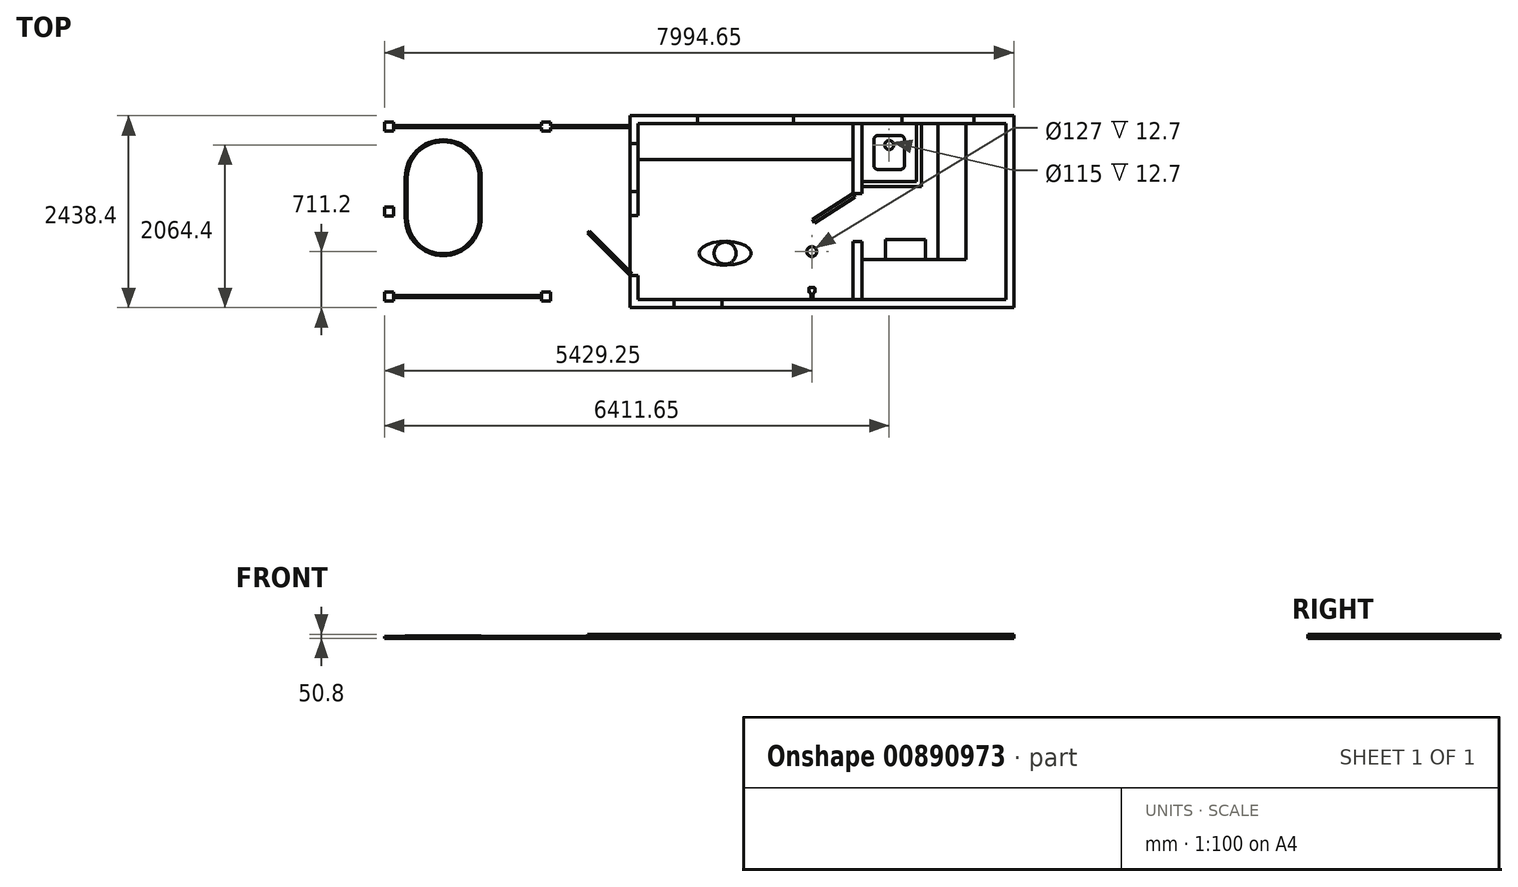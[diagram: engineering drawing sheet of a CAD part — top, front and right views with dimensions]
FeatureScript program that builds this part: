
annotation { "Feature Type Name" : "Feature", "Feature Type Description" : "" }
export const myFeature = defineFeature(function(context is Context, id is Id, definition is map)
    precondition{}
    {
        {
            var Q0;
            Q0=qCreatedBy(makeId("Top.planeOp"),FACE);
            var sketch = newSketch(context, id + "F0", { "sketchPlane" : qUnion([Q0])});
            skLineSegment(sketch, "E0.bottom", {"start": v(-2438.4, -1219.2) * mm, "end": v(2438.4, -1219.2) * mm});
            skLineSegment(sketch, "E0.top", {"start": v(-2438.4, 1219.2) * mm, "end": v(2438.4, 1219.2) * mm});
            skLineSegment(sketch, "E0.left", {"start": v(-2438.4, -1219.2) * mm, "end": v(-2438.4, 1219.2) * mm});
            skLineSegment(sketch, "E0.right", {"start": v(2438.4, -1219.2) * mm, "end": v(2438.4, 1219.2) * mm});
            skPoint(sketch, "E0.middle", {"position": v(0, 0) * mm});
            skSolve(sketch);
        }
        {
            var Q0;
            Q0=qSketchRegion(id+"F0",true);
            extrude(context, id + "F1", {"entities" : qUnion([Q0]), "depth" : 25.4 * mm, "offsetDistance" : 25.4 * mm});
        }
        {
            var Q0;
            Q0=makeQuery(id+"F1.opExtrude","CAP_FACE",FACE,{"disambiguationData":[OSD([sQuery(id+"F0.wireOp",EDGE,"E0.bottom"),sQuery(id+"F0.wireOp",EDGE,"E0.top"),sQuery(id+"F0.wireOp",EDGE,"E0.left"),sQuery(id+"F0.wireOp",EDGE,"E0.right")])],"isStart":false});
            var sketch = newSketch(context, id + "F2", { "sketchPlane" : qUnion([Q0])});
            skLineSegment(sketch, "E1.0", {"start": v(-2438.4, 1219.2) * mm, "end": v(2438.4, 1219.2) * mm});
            skLineSegment(sketch, "E2.0", {"start": v(-2438.4, -1219.2) * mm, "end": v(-2438.4, 1219.2) * mm});
            skLineSegment(sketch, "E3.0", {"start": v(-2438.4, -1219.2) * mm, "end": v(2438.4, -1219.2) * mm});
            skLineSegment(sketch, "E4.0", {"start": v(2438.4, -1219.2) * mm, "end": v(2438.4, 1219.2) * mm});
            skLineSegment(sketch, "E5.bottom", {"start": v(-2336.8, 1117.6) * mm, "end": v(2336.8, 1117.6) * mm});
            skLineSegment(sketch, "E5.top", {"start": v(-2336.8, -1117.6) * mm, "end": v(2336.8, -1117.6) * mm});
            skLineSegment(sketch, "E5.left", {"start": v(-2336.8, 1117.6) * mm, "end": v(-2336.8, -1117.6) * mm});
            skLineSegment(sketch, "E5.right", {"start": v(2336.8, 1117.6) * mm, "end": v(2336.8, -1117.6) * mm});
            skPoint(sketch, "E5.middle", {"position": v(0, 0) * mm});
            skSolve(sketch);
        }
        {
            var Q0;
            Q0=qSketchRegion(id+"F2",true);
            extrude(context, id + "F3", {"entities" : qUnion([Q0]), "depth" : 25.4 * mm, "offsetDistance" : 25.4 * mm});
        }
        {
            var Q0;
            Q0=makeQuery(id+"F1.opExtrude","CAP_FACE",FACE,{"disambiguationData":[OSD([sQuery(id+"F0.wireOp",EDGE,"E0.bottom"),sQuery(id+"F0.wireOp",EDGE,"E0.top"),sQuery(id+"F0.wireOp",EDGE,"E0.left"),sQuery(id+"F0.wireOp",EDGE,"E0.right")])],"isStart":false});
            var sketch = newSketch(context, id + "F4", { "sketchPlane" : qUnion([Q0])});
            skLineSegment(sketch, "E6.bottom", {"start": v(393.7, 1117.6) * mm, "end": v(508, 1117.6) * mm});
            skLineSegment(sketch, "E6.top", {"start": v(393.7, -1117.6) * mm, "end": v(508, -1117.6) * mm});
            skLineSegment(sketch, "E6.left", {"start": v(393.7, 1117.6) * mm, "end": v(393.7, -1117.6) * mm});
            skLineSegment(sketch, "E6.right", {"start": v(508, 1117.6) * mm, "end": v(508, -1117.6) * mm});
            skSolve(sketch);
        }
        {
            var Q0;
            Q0=qSketchRegion(id+"F4",true);
            extrude(context, id + "F5", {"entities" : qUnion([Q0]), "depth" : 25.4 * mm, "offsetDistance" : 25.4 * mm});
        }
        {
            var Q0;
            Q0=makeQuery(id+"F5.opExtrude","CAP_FACE",FACE,{"disambiguationData":[OSD([sQuery(id+"F4.wireOp",EDGE,"E6.bottom"),sQuery(id+"F4.wireOp",EDGE,"E6.top"),sQuery(id+"F4.wireOp",EDGE,"E6.left"),sQuery(id+"F4.wireOp",EDGE,"E6.right")])],"isStart":false});
            var sketch = newSketch(context, id + "F6", { "sketchPlane" : qUnion([Q0])});
            skLineSegment(sketch, "E7.bottom", {"start": v(393.7, 228.6) * mm, "end": v(508, 228.6) * mm});
            skLineSegment(sketch, "E7.top", {"start": v(393.7, -381) * mm, "end": v(508, -381) * mm});
            skLineSegment(sketch, "E7.left", {"start": v(393.7, 228.6) * mm, "end": v(393.7, -381) * mm});
            skLineSegment(sketch, "E7.right", {"start": v(508, 228.6) * mm, "end": v(508, -381) * mm});
            skSolve(sketch);
        }
        {
            var Q0;
            Q0=qSketchRegion(id+"F6",true);
            extrude(context, id + "F7", {"entities" : qUnion([Q0]), "operationType" : NewBodyOperationType.REMOVE, "oppositeDirection" : true, "depth" : 25.4 * mm, "offsetDistance" : 25.4 * mm});
        }
        {
            var Q0;
            Q0=makeQuery(id+"F3.opExtrude","CAP_FACE",FACE,{"disambiguationData":[OSD([sQuery(id+"F2.wireOp",EDGE,"E1.0"),sQuery(id+"F2.wireOp",EDGE,"E2.0"),sQuery(id+"F2.wireOp",EDGE,"E3.0"),sQuery(id+"F2.wireOp",EDGE,"E4.0"),sQuery(id+"F2.wireOp",EDGE,"E5.bottom"),sQuery(id+"F2.wireOp",EDGE,"E5.top"),sQuery(id+"F2.wireOp",EDGE,"E5.left"),sQuery(id+"F2.wireOp",EDGE,"E5.right")])],"isStart":false});
            var sketch = newSketch(context, id + "F8", { "sketchPlane" : qUnion([Q0])});
            skLineSegment(sketch, "E8.bottom", {"start": v(-2438.4, -812.8) * mm, "end": v(-2336.8, -812.8) * mm});
            skLineSegment(sketch, "E8.top", {"start": v(-2438.4, -50.8) * mm, "end": v(-2336.8, -50.8) * mm});
            skLineSegment(sketch, "E8.left", {"start": v(-2438.4, -812.8) * mm, "end": v(-2438.4, -50.8) * mm});
            skLineSegment(sketch, "E8.right", {"start": v(-2336.8, -812.8) * mm, "end": v(-2336.8, -50.8) * mm});
            skSolve(sketch);
        }
        {
            var Q0;
            Q0=qSketchRegion(id+"F8",true);
            extrude(context, id + "F9", {"entities" : qUnion([Q0]), "operationType" : NewBodyOperationType.REMOVE, "oppositeDirection" : true, "depth" : 25.4 * mm, "offsetDistance" : 25.4 * mm});
        }
        {
            var Q0;
            Q0=makeQuery(id+"F1.opExtrude","CAP_FACE",FACE,{"disambiguationData":[OSD([sQuery(id+"F0.wireOp",EDGE,"E0.bottom"),sQuery(id+"F0.wireOp",EDGE,"E0.top"),sQuery(id+"F0.wireOp",EDGE,"E0.left"),sQuery(id+"F0.wireOp",EDGE,"E0.right")])],"isStart":false});
            var sketch = newSketch(context, id + "F10", { "sketchPlane" : qUnion([Q0])});
            skLineSegment(sketch, "E9.bottom", {"start": v(711.2, 965.2) * mm, "end": v(999.6, 965.2) * mm});
            skLineSegment(sketch, "E9.top", {"start": v(711.2, 535.2) * mm, "end": v(999.6, 535.2) * mm});
            skLineSegment(sketch, "E9.left", {"start": v(660.4, 914.4) * mm, "end": v(660.4, 586) * mm});
            skLineSegment(sketch, "E9.right", {"start": v(1050.4, 914.4) * mm, "end": v(1050.4, 586) * mm});
            skPoint(sketch, "E10.visualSharp", {"position": v(660.4, 965.2) * mm});
            skArc(sketch, "E10.filletArc", {"start": v(711.2, 965.2) * mm, "mid": v(675.28, 950.32) * mm, "end": v(660.4, 914.4) * mm});
            skPoint(sketch, "E11.visualSharp", {"position": v(1050.4, 965.2) * mm});
            skArc(sketch, "E11.filletArc", {"start": v(1050.4, 914.4) * mm, "mid": v(1035.52, 950.32) * mm, "end": v(999.6, 965.2) * mm});
            skPoint(sketch, "E12.visualSharp", {"position": v(1050.4, 535.2) * mm});
            skArc(sketch, "E12.filletArc", {"start": v(999.6, 535.2) * mm, "mid": v(1035.52, 550.08) * mm, "end": v(1050.4, 586) * mm});
            skPoint(sketch, "E13.visualSharp", {"position": v(660.4, 535.2) * mm});
            skArc(sketch, "E13.filletArc", {"start": v(660.4, 586) * mm, "mid": v(675.28, 550.08) * mm, "end": v(711.2, 535.2) * mm});
            skSolve(sketch);
        }
        {
            var Q0;
            Q0=qSketchRegion(id+"F10",true);
            extrude(context, id + "F11", {"entities" : qUnion([Q0]), "depth" : 25.4 * mm, "offsetDistance" : 25.4 * mm});
        }
        {
            var Q0;
            Q0=makeQuery(id+"F1.opExtrude","CAP_FACE",FACE,{"disambiguationData":[OSD([sQuery(id+"F0.wireOp",EDGE,"E0.bottom"),sQuery(id+"F0.wireOp",EDGE,"E0.top"),sQuery(id+"F0.wireOp",EDGE,"E0.left"),sQuery(id+"F0.wireOp",EDGE,"E0.right")])],"isStart":false});
            var sketch = newSketch(context, id + "F12", { "sketchPlane" : qUnion([Q0])});
            skLineSegment(sketch, "E14", {"start": v(508, -1117.6) * mm, "end": v(2336.8, -1117.6) * mm});
            skLineSegment(sketch, "E15", {"start": v(2336.8, -1117.6) * mm, "end": v(2336.8, 1117.6) * mm});
            skLineSegment(sketch, "E16", {"start": v(2336.8, 1117.6) * mm, "end": v(1828.8, 1117.6) * mm});
            skLineSegment(sketch, "E17", {"start": v(1828.8, 1117.6) * mm, "end": v(1828.8, -609.6) * mm});
            skLineSegment(sketch, "E18", {"start": v(1828.8, -609.6) * mm, "end": v(508, -609.6) * mm});
            skLineSegment(sketch, "E19", {"start": v(508, -609.6) * mm, "end": v(508, -1117.6) * mm});
            skSolve(sketch);
        }
        {
            var Q0;
            Q0=qSketchRegion(id+"F12",true);
            extrude(context, id + "F13", {"entities" : qUnion([Q0]), "depth" : 25.4 * mm, "offsetDistance" : 25.4 * mm});
        }
        {
            var Q0;
            Q0=makeQuery(id+"F1.opExtrude","CAP_FACE",FACE,{"disambiguationData":[OSD([sQuery(id+"F0.wireOp",EDGE,"E0.bottom"),sQuery(id+"F0.wireOp",EDGE,"E0.top"),sQuery(id+"F0.wireOp",EDGE,"E0.left"),sQuery(id+"F0.wireOp",EDGE,"E0.right")])],"isStart":false});
            var sketch = newSketch(context, id + "F14", { "sketchPlane" : qUnion([Q0])});
            skLineSegment(sketch, "E20.0", {"start": v(1828.8, -609.6) * mm, "end": v(1473.2, -609.6) * mm});
            skLineSegment(sketch, "E21.0", {"start": v(1828.8, 1117.6) * mm, "end": v(1828.8, -609.6) * mm});
            skLineSegment(sketch, "E22", {"start": v(1473.2, -609.6) * mm, "end": v(1473.2, 1117.6) * mm});
            skLineSegment(sketch, "E23", {"start": v(1473.2, 1117.6) * mm, "end": v(1828.8, 1117.6) * mm});
            skSolve(sketch);
        }
        {
            var Q0;
            Q0=qSketchRegion(id+"F14",true);
            extrude(context, id + "F15", {"entities" : qUnion([Q0]), "depth" : 12.7 * mm, "offsetDistance" : 25.4 * mm});
        }
        {
            var Q0;
            Q0=makeQuery(id+"F1.opExtrude","CAP_FACE",FACE,{"disambiguationData":[OSD([sQuery(id+"F0.wireOp",EDGE,"E0.bottom"),sQuery(id+"F0.wireOp",EDGE,"E0.top"),sQuery(id+"F0.wireOp",EDGE,"E0.left"),sQuery(id+"F0.wireOp",EDGE,"E0.right")])],"isStart":false});
            var sketch = newSketch(context, id + "F16", { "sketchPlane" : qUnion([Q0])});
            skLineSegment(sketch, "E24.bottom", {"start": v(393.7, 228.6) * mm, "end": v(-117.99, -102.75) * mm});
            skLineSegment(sketch, "E24.top", {"start": v(421.31, 185.96) * mm, "end": v(-90.37, -145.39) * mm});
            skLineSegment(sketch, "E24.left", {"start": v(393.7, 228.6) * mm, "end": v(421.31, 185.96) * mm});
            skLineSegment(sketch, "E24.right", {"start": v(-117.99, -102.75) * mm, "end": v(-90.37, -145.39) * mm});
            skSolve(sketch);
        }
        {
            var Q0;
            Q0=qSketchRegion(id+"F16",true);
            extrude(context, id + "F17", {"entities" : qUnion([Q0]), "depth" : 25.4 * mm, "offsetDistance" : 25.4 * mm});
        }
        {
            var Q0;
            Q0=makeQuery(id+"F1.opExtrude","CAP_FACE",FACE,{"disambiguationData":[OSD([sQuery(id+"F0.wireOp",EDGE,"E0.bottom"),sQuery(id+"F0.wireOp",EDGE,"E0.top"),sQuery(id+"F0.wireOp",EDGE,"E0.left"),sQuery(id+"F0.wireOp",EDGE,"E0.right")])],"isStart":false});
            var sketch = newSketch(context, id + "F18", { "sketchPlane" : qUnion([Q0])});
            skLineSegment(sketch, "E25.bottom", {"start": v(-2411.46, -785.86) * mm, "end": v(-2438.4, -812.8) * mm});
            skLineSegment(sketch, "E25.top", {"start": v(-2950.27, -247.04) * mm, "end": v(-2977.22, -273.98) * mm});
            skLineSegment(sketch, "E25.left", {"start": v(-2950.27, -247.04) * mm, "end": v(-2411.46, -785.86) * mm});
            skLineSegment(sketch, "E25.right", {"start": v(-2977.22, -273.98) * mm, "end": v(-2438.4, -812.8) * mm});
            skSolve(sketch);
        }
        {
            var Q0;
            Q0=qSketchRegion(id+"F18",true);
            extrude(context, id + "F19", {"entities" : qUnion([Q0]), "depth" : 25.4 * mm, "offsetDistance" : 25.4 * mm});
        }
        {
            var Q0;
            Q0=makeQuery(id+"F1.opExtrude","CAP_FACE",FACE,{"disambiguationData":[OSD([sQuery(id+"F0.wireOp",EDGE,"E0.bottom"),sQuery(id+"F0.wireOp",EDGE,"E0.top"),sQuery(id+"F0.wireOp",EDGE,"E0.left"),sQuery(id+"F0.wireOp",EDGE,"E0.right")])],"isStart":false});
            var sketch = newSketch(context, id + "F20", { "sketchPlane" : qUnion([Q0])});
            skCircle(sketch, "E26", {"center": v(-127, -508) * mm, "radius": 63.5 * mm});
            skSolve(sketch);
        }
        {
            var Q0;
            Q0=qSketchRegion(id+"F20",true);
            extrude(context, id + "F21", {"entities" : qUnion([Q0]), "operationType" : NewBodyOperationType.REMOVE, "oppositeDirection" : true, "depth" : 12.7 * mm, "offsetDistance" : 25.4 * mm});
        }
        {
            var Q0;
            Q0=makeQuery(id+"F1.opExtrude","CAP_FACE",FACE,{"disambiguationData":[OSD([sQuery(id+"F0.wireOp",EDGE,"E0.bottom"),sQuery(id+"F0.wireOp",EDGE,"E0.top"),sQuery(id+"F0.wireOp",EDGE,"E0.left"),sQuery(id+"F0.wireOp",EDGE,"E0.right")])],"isStart":false});
            var sketch = newSketch(context, id + "F22", { "sketchPlane" : qUnion([Q0])});
            skLineSegment(sketch, "E27", {"start": v(-139.7, -1117.6) * mm, "end": v(-139.7, -1028.7) * mm});
            skLineSegment(sketch, "E28", {"start": v(-139.7, -1028.7) * mm, "end": v(-158.75, -1028.7) * mm});
            skLineSegment(sketch, "E29", {"start": v(-165.1, -1022.35) * mm, "end": v(-165.1, -971.55) * mm});
            skLineSegment(sketch, "E30", {"start": v(-158.75, -965.2) * mm, "end": v(-95.25, -965.2) * mm});
            skLineSegment(sketch, "E31", {"start": v(-88.9, -971.55) * mm, "end": v(-88.9, -1022.35) * mm});
            skLineSegment(sketch, "E32", {"start": v(-95.25, -1028.7) * mm, "end": v(-114.3, -1028.7) * mm});
            skLineSegment(sketch, "E33", {"start": v(-114.3, -1028.7) * mm, "end": v(-114.3, -1117.6) * mm});
            skLineSegment(sketch, "E34", {"start": v(-114.3, -1117.6) * mm, "end": v(-139.7, -1117.6) * mm});
            skPoint(sketch, "E35.visualSharp", {"position": v(-165.1, -965.2) * mm});
            skArc(sketch, "E35.filletArc", {"start": v(-158.75, -965.2) * mm, "mid": v(-163.24, -967.06) * mm, "end": v(-165.1, -971.55) * mm});
            skPoint(sketch, "E36.visualSharp", {"position": v(-165.1, -1028.7) * mm});
            skArc(sketch, "E36.filletArc", {"start": v(-165.1, -1022.35) * mm, "mid": v(-163.24, -1026.84) * mm, "end": v(-158.75, -1028.7) * mm});
            skPoint(sketch, "E37.visualSharp", {"position": v(-88.9, -1028.7) * mm});
            skArc(sketch, "E37.filletArc", {"start": v(-95.25, -1028.7) * mm, "mid": v(-90.76, -1026.84) * mm, "end": v(-88.9, -1022.35) * mm});
            skPoint(sketch, "E38.visualSharp", {"position": v(-88.9, -965.2) * mm});
            skArc(sketch, "E38.filletArc", {"start": v(-88.9, -971.55) * mm, "mid": v(-90.76, -967.06) * mm, "end": v(-95.25, -965.2) * mm});
            skSolve(sketch);
        }
        {
            var Q0;
            Q0=qSketchRegion(id+"F22",true);
            extrude(context, id + "F23", {"entities" : qUnion([Q0]), "depth" : 12.7 * mm, "offsetDistance" : 25.4 * mm});
        }
        {
            var Q0;
            Q0=makeQuery(id+"F1.opExtrude","CAP_FACE",FACE,{"disambiguationData":[OSD([sQuery(id+"F0.wireOp",EDGE,"E0.bottom"),sQuery(id+"F0.wireOp",EDGE,"E0.top"),sQuery(id+"F0.wireOp",EDGE,"E0.left"),sQuery(id+"F0.wireOp",EDGE,"E0.right")])],"isStart":false});
            var sketch = newSketch(context, id + "F24", { "sketchPlane" : qUnion([Q0])});
            skLineSegment(sketch, "E39", {"start": v(-2336.8, 660.4) * mm, "end": v(-2336.8, 1117.6) * mm});
            skLineSegment(sketch, "E40", {"start": v(-2336.8, 1117.6) * mm, "end": v(393.7, 1117.6) * mm});
            skLineSegment(sketch, "E41", {"start": v(393.7, 1117.6) * mm, "end": v(393.7, 660.4) * mm});
            skLineSegment(sketch, "E42", {"start": v(393.7, 660.4) * mm, "end": v(-2336.8, 660.4) * mm});
            skSolve(sketch);
        }
        {
            var Q0;
            Q0=qSketchRegion(id+"F24",true);
            extrude(context, id + "F25", {"entities" : qUnion([Q0]), "depth" : 25.4 * mm, "offsetDistance" : 25.4 * mm});
        }
        {
            var Q0;
            Q0=makeQuery(id+"F3.opExtrude","CAP_FACE",FACE,{"disambiguationData":[OSD([sQuery(id+"F2.wireOp",EDGE,"E1.0"),sQuery(id+"F2.wireOp",EDGE,"E2.0"),sQuery(id+"F2.wireOp",EDGE,"E3.0"),sQuery(id+"F2.wireOp",EDGE,"E4.0"),sQuery(id+"F2.wireOp",EDGE,"E5.bottom"),sQuery(id+"F2.wireOp",EDGE,"E5.top"),sQuery(id+"F2.wireOp",EDGE,"E5.left"),sQuery(id+"F2.wireOp",EDGE,"E5.right")])],"isStart":false});
            var sketch = newSketch(context, id + "F26", { "sketchPlane" : qUnion([Q0])});
            skLineSegment(sketch, "E43.bottom", {"start": v(-1879.6, -1117.6) * mm, "end": v(-1270, -1117.6) * mm});
            skLineSegment(sketch, "E43.top", {"start": v(-1879.6, -1219.2) * mm, "end": v(-1270, -1219.2) * mm});
            skLineSegment(sketch, "E43.left", {"start": v(-1879.6, -1117.6) * mm, "end": v(-1879.6, -1219.2) * mm});
            skLineSegment(sketch, "E43.right", {"start": v(-1270, -1117.6) * mm, "end": v(-1270, -1219.2) * mm});
            skLineSegment(sketch, "E44.bottom", {"start": v(-2438.4, 863.6) * mm, "end": v(-2336.8, 863.6) * mm});
            skLineSegment(sketch, "E44.top", {"start": v(-2438.4, 254) * mm, "end": v(-2336.8, 254) * mm});
            skLineSegment(sketch, "E44.left", {"start": v(-2438.4, 863.6) * mm, "end": v(-2438.4, 254) * mm});
            skLineSegment(sketch, "E44.right", {"start": v(-2336.8, 863.6) * mm, "end": v(-2336.8, 254) * mm});
            skSolve(sketch);
        }
        {
            var Q0;
            Q0=qSketchRegion(id+"F26",true);
            extrude(context, id + "F27", {"entities" : qUnion([Q0]), "operationType" : NewBodyOperationType.REMOVE, "oppositeDirection" : true, "depth" : 12.7 * mm, "offsetDistance" : 25.4 * mm});
        }
        {
            var Q0;
            Q0=makeQuery(id+"F11.opExtrude","CAP_FACE",FACE,{"disambiguationData":[OSD([sQuery(id+"F10.wireOp",EDGE,"E9.bottom"),sQuery(id+"F10.wireOp",EDGE,"E9.top"),sQuery(id+"F10.wireOp",EDGE,"E9.left"),sQuery(id+"F10.wireOp",EDGE,"E9.right"),sQuery(id+"F10.wireOp",EDGE,"E10.filletArc"),sQuery(id+"F10.wireOp",EDGE,"E11.filletArc"),sQuery(id+"F10.wireOp",EDGE,"E12.filletArc"),sQuery(id+"F10.wireOp",EDGE,"E13.filletArc")])],"isStart":false});
            var sketch = newSketch(context, id + "F28", { "sketchPlane" : qUnion([Q0])});
            skCircle(sketch, "E45", {"center": v(855.4, 845.2) * mm, "radius": 57.5 * mm});
            skLineSegment(sketch, "E46", {"start": v(855.4, 965.2) * mm, "end": v(855.4, 845.2) * mm, "construction": true});
            skSolve(sketch);
        }
        {
            var Q0;
            Q0=qSketchRegion(id+"F28",true);
            extrude(context, id + "F29", {"entities" : qUnion([Q0]), "operationType" : NewBodyOperationType.REMOVE, "oppositeDirection" : true, "depth" : 12.7 * mm, "offsetDistance" : 25.4 * mm});
        }
        {
            var Q0;
            Q0=qCreatedBy(makeId("Top.planeOp"),FACE);
            var sketch = newSketch(context, id + "F30", { "sketchPlane" : qUnion([Q0])});
            skLineSegment(sketch, "E47.bottom", {"start": v(-5441.95, 1022.35) * mm, "end": v(-5556.25, 1022.35) * mm});
            skLineSegment(sketch, "E47.top", {"start": v(-5441.95, 1136.65) * mm, "end": v(-5556.25, 1136.65) * mm});
            skLineSegment(sketch, "E47.left", {"start": v(-5441.95, 1022.35) * mm, "end": v(-5441.95, 1136.65) * mm});
            skLineSegment(sketch, "E47.right", {"start": v(-5556.25, 1022.35) * mm, "end": v(-5556.25, 1136.65) * mm});
            skPoint(sketch, "E47.middle", {"position": v(-5499.1, 1079.5) * mm});
            skLineSegment(sketch, "E48.bottom", {"start": v(-5441.95, -57.15) * mm, "end": v(-5556.25, -57.15) * mm});
            skLineSegment(sketch, "E48.top", {"start": v(-5441.95, 57.15) * mm, "end": v(-5556.25, 57.15) * mm});
            skLineSegment(sketch, "E48.left", {"start": v(-5441.95, -57.15) * mm, "end": v(-5441.95, 57.15) * mm});
            skLineSegment(sketch, "E48.right", {"start": v(-5556.25, -57.15) * mm, "end": v(-5556.25, 57.15) * mm});
            skPoint(sketch, "E48.middle", {"position": v(-5499.1, 0) * mm});
            skLineSegment(sketch, "E49.bottom", {"start": v(-5441.95, -1136.65) * mm, "end": v(-5556.25, -1136.65) * mm});
            skLineSegment(sketch, "E49.top", {"start": v(-5441.95, -1022.35) * mm, "end": v(-5556.25, -1022.35) * mm});
            skLineSegment(sketch, "E49.left", {"start": v(-5441.95, -1136.65) * mm, "end": v(-5441.95, -1022.35) * mm});
            skLineSegment(sketch, "E49.right", {"start": v(-5556.25, -1136.65) * mm, "end": v(-5556.25, -1022.35) * mm});
            skPoint(sketch, "E49.middle", {"position": v(-5499.1, -1079.5) * mm});
            skLineSegment(sketch, "E50.bottom", {"start": v(-5441.95, 1092.2) * mm, "end": v(-3562.35, 1092.2) * mm});
            skLineSegment(sketch, "E50.top", {"start": v(-5441.95, 1066.8) * mm, "end": v(-3562.35, 1066.8) * mm});
            skLineSegment(sketch, "E50.left", {"start": v(-5441.95, 1092.2) * mm, "end": v(-5441.95, 1066.8) * mm});
            skPoint(sketch, "E50.middle", {"position": v(-3940.17, 1079.5) * mm});
            skLineSegment(sketch, "E51.bottom", {"start": v(-5486.4, 1022.35) * mm, "end": v(-5511.8, 1022.35) * mm});
            skLineSegment(sketch, "E51.top", {"start": v(-5486.4, 57.15) * mm, "end": v(-5511.8, 57.15) * mm});
            skLineSegment(sketch, "E51.left", {"start": v(-5486.4, 1022.35) * mm, "end": v(-5486.4, 57.15) * mm});
            skLineSegment(sketch, "E51.right", {"start": v(-5511.8, 1022.35) * mm, "end": v(-5511.8, 57.15) * mm});
            skPoint(sketch, "E51.middle", {"position": v(-5499.1, 539.75) * mm});
            skLineSegment(sketch, "E52.bottom", {"start": v(-5511.8, -1022.35) * mm, "end": v(-5486.4, -1022.35) * mm});
            skLineSegment(sketch, "E52.top", {"start": v(-5511.8, -57.15) * mm, "end": v(-5486.4, -57.15) * mm});
            skLineSegment(sketch, "E52.left", {"start": v(-5511.8, -1022.35) * mm, "end": v(-5511.8, -57.15) * mm});
            skLineSegment(sketch, "E52.right", {"start": v(-5486.4, -1022.35) * mm, "end": v(-5486.4, -57.15) * mm});
            skPoint(sketch, "E52.middle", {"position": v(-5499.1, -539.75) * mm});
            skLineSegment(sketch, "E53.bottom", {"start": v(-5441.95, -1066.8) * mm, "end": v(-3562.35, -1066.8) * mm});
            skLineSegment(sketch, "E53.top", {"start": v(-5441.95, -1092.2) * mm, "end": v(-3562.35, -1092.2) * mm});
            skLineSegment(sketch, "E53.left", {"start": v(-5441.95, -1066.8) * mm, "end": v(-5441.95, -1092.2) * mm});
            skLineSegment(sketch, "E53.right", {"start": v(-3562.35, -1066.8) * mm, "end": v(-3562.35, -1092.2) * mm});
            skPoint(sketch, "E53.middle", {"position": v(-4502.15, -1079.5) * mm});
            skLineSegment(sketch, "E54.bottom", {"start": v(-3448.05, -1136.65) * mm, "end": v(-3562.35, -1136.65) * mm});
            skLineSegment(sketch, "E54.top", {"start": v(-3448.05, -1022.35) * mm, "end": v(-3562.35, -1022.35) * mm});
            skLineSegment(sketch, "E54.left", {"start": v(-3448.05, -1136.65) * mm, "end": v(-3448.05, -1022.35) * mm});
            skLineSegment(sketch, "E54.right", {"start": v(-3562.35, -1136.65) * mm, "end": v(-3562.35, -1022.35) * mm});
            skPoint(sketch, "E54.middle", {"position": v(-3505.2, -1079.5) * mm});
            skLineSegment(sketch, "E55", {"start": v(-2438.4, 1092.2) * mm, "end": v(-2438.4, 1066.8) * mm});
            skPoint(sketch, "E56", {"position": v(-5441.95, 1079.5) * mm});
            skLineSegment(sketch, "E57.bottom", {"start": v(-3448.05, 1022.35) * mm, "end": v(-3562.35, 1022.35) * mm});
            skLineSegment(sketch, "E57.top", {"start": v(-3448.05, 1136.65) * mm, "end": v(-3562.35, 1136.65) * mm});
            skLineSegment(sketch, "E57.left", {"start": v(-3448.05, 1022.35) * mm, "end": v(-3448.05, 1136.65) * mm});
            skLineSegment(sketch, "E57.right", {"start": v(-3562.35, 1022.35) * mm, "end": v(-3562.35, 1136.65) * mm});
            skPoint(sketch, "E57.middle", {"position": v(-3505.2, 1079.5) * mm});
            skLineSegment(sketch, "E58.trimOffspring", {"start": v(-3448.05, 1066.8) * mm, "end": v(-2438.4, 1066.8) * mm});
            skLineSegment(sketch, "E59.trimOffspring", {"start": v(-3448.05, 1092.2) * mm, "end": v(-2438.4, 1092.2) * mm});
            skLineSegment(sketch, "E60", {"start": v(-3562.35, 1092.2) * mm, "end": v(-3562.35, 1066.8) * mm});
            skLineSegment(sketch, "E61", {"start": v(-3448.05, 1092.2) * mm, "end": v(-3448.05, 1066.8) * mm});
            skSolve(sketch);
        }
        {
            var Q0;
            {var subQ1=sQuery(id+"F30.wireOp",EDGE,"E49.bottom");Q0=makeQuery(id+"F30.imprint","IMPRINT",FACE,{"disambiguationData":[TD([[makeQuery(id+"F30.imprint","IMPRINT",EDGE,{"derivedFrom":subQ1}),-1.0]])]});}
            var Q1;
            {var subQ2=sQuery(id+"F30.wireOp",EDGE,"E54.bottom");Q1=makeQuery(id+"F30.imprint","IMPRINT",FACE,{"disambiguationData":[TD([[makeQuery(id+"F30.imprint","IMPRINT",EDGE,{"derivedFrom":subQ2}),-1.0]])]});}
            var Q2;
            {var subQ3=sQuery(id+"F30.wireOp",EDGE,"E48.left");Q2=makeQuery(id+"F30.imprint","IMPRINT",FACE,{"disambiguationData":[TD([[makeQuery(id+"F30.imprint","IMPRINT",EDGE,{"derivedFrom":subQ3}),1.0]])]});}
            var Q3;
            {var subQ4=sQuery(id+"F30.wireOp",EDGE,"E47.top");Q3=makeQuery(id+"F30.imprint","IMPRINT",FACE,{"disambiguationData":[TD([[makeQuery(id+"F30.imprint","IMPRINT",EDGE,{"derivedFrom":subQ4}),1.0]])]});}
            var Q4;
            {var subQ2=sQuery(id+"F30.wireOp",EDGE,"tz3fCbJH-QJVn-jlAM-z3Om-JQKKFmsdvTRM.top");Q4=makeQuery(id+"F30.imprint","IMPRINT",FACE,{"disambiguationData":[TD([[makeQuery(id+"F30.imprint","IMPRINT",EDGE,{"derivedFrom":subQ2}),1.0]])]});}
            extrude(context, id + "F31", {"entities" : qUnion([Q0, Q1, Q2, Q3, Q4]), "depth" : 25.4 * mm, "offsetDistance" : 25.4 * mm});
        }
        {
            var Q0;
            {var subQ0=sQuery(id+"F30.wireOp",EDGE,"E53.bottom");Q0=makeQuery(id+"F30.imprint","IMPRINT",FACE,{"disambiguationData":[TD([[makeQuery(id+"F30.imprint","IMPRINT",EDGE,{"derivedFrom":subQ0}),-1.0]])]});}
            var Q1;
            Q1=makeQuery(id+"F30.imprint","IMPRINT",FACE,{"disambiguationData":[TD([[makeQuery(id+"F30.imprint","IMPRINT",EDGE,{"derivedFrom":sQuery(id+"F30.wireOp",EDGE,"E52.bottom")}),1.0]])]});
            var Q2;
            Q2=makeQuery(id+"F30.imprint","IMPRINT",FACE,{"disambiguationData":[TD([[makeQuery(id+"F30.imprint","IMPRINT",EDGE,{"derivedFrom":sQuery(id+"F30.wireOp",EDGE,"E51.bottom")}),1.0]])]});
            var Q3;
            Q3=makeQuery(id+"F30.imprint","IMPRINT",FACE,{"disambiguationData":[TD([[makeQuery(id+"F30.imprint","IMPRINT",EDGE,{"derivedFrom":sQuery(id+"F30.wireOp",EDGE,"E50.bottom")}),-1.0]])]});
            var Q4;
            Q4=makeQuery(id+"F30.imprint","IMPRINT",FACE,{"disambiguationData":[TD([[makeQuery(id+"F30.imprint","IMPRINT",EDGE,{"derivedFrom":sQuery(id+"F30.wireOp",EDGE,"l0aV7X77-QWTU-Nury-uGZZ-4KhOBLiAyjhT.bottom")}),1.0]])]});
            var Q5;
            {var subQ3=sQuery(id+"F30.wireOp",EDGE,"E57.bottom");Q5=makeQuery(id+"F30.imprint","IMPRINT",FACE,{"disambiguationData":[TD([[makeQuery(id+"F30.imprint","IMPRINT",EDGE,{"derivedFrom":subQ3}),-1.0]])]});}
            var Q6;
            Q6=makeQuery(id+"F30.imprint","IMPRINT",FACE,{"disambiguationData":[TD([[makeQuery(id+"F30.imprint","IMPRINT",EDGE,{"derivedFrom":sQuery(id+"F30.wireOp",EDGE,"E55")}),-1.0]])]});
            extrude(context, id + "F32", {"entities" : qUnion([Q0, Q1, Q2, Q3, Q4, Q5, Q6]), "depth" : 25.4 * mm, "offsetDistance" : 25.4 * mm});
        }
        {
            var Q0;
            Q0=makeQuery(id+"F1.opExtrude","CAP_FACE",FACE,{"disambiguationData":[OSD([sQuery(id+"F0.wireOp",EDGE,"E0.bottom"),sQuery(id+"F0.wireOp",EDGE,"E0.top"),sQuery(id+"F0.wireOp",EDGE,"E0.left"),sQuery(id+"F0.wireOp",EDGE,"E0.right")])],"isStart":false});
            var sketch = newSketch(context, id + "F33", { "sketchPlane" : qUnion([Q0])});
            skCircle(sketch, "E62", {"center": v(-1228.45, -528.59) * mm, "radius": 139.7 * mm});
            skEllipse(sketch, "E63", {"center": v(-1228.45, -528.59) * mm, "majorRadius": 330.2 * mm, "minorRadius": 152.4 * mm, "majorAxis": v(-1, 0)});
            skSolve(sketch);
        }
        {
            var Q0;
            Q0=makeQuery(id+"F33.imprint","IMPRINT",FACE,{"disambiguationData":[TD([[makeQuery(id+"F33.imprint","IMPRINT",EDGE,{"derivedFrom":sQuery(id+"F33.wireOp",EDGE,"E62")}),1.0]])]});
            extrude(context, id + "F34", {"entities" : qUnion([Q0]), "operationType" : NewBodyOperationType.ADD, "depth" : 25.4 * mm, "offsetDistance" : 25.4 * mm});
        }
        {
            var Q0;
            Q0=makeQuery(id+"F33.imprint","IMPRINT",FACE,{"disambiguationData":[TD([[makeQuery(id+"F33.imprint","IMPRINT",EDGE,{"derivedFrom":sQuery(id+"F33.wireOp",EDGE,"E62")}),-1.0]])]});
            extrude(context, id + "F35", {"entities" : qUnion([Q0]), "operationType" : NewBodyOperationType.ADD, "depth" : 12.7 * mm, "offsetDistance" : 25.4 * mm});
        }
        {
            var Q0;
            Q0=qCreatedBy(makeId("Top.planeOp"),FACE);
            var sketch = newSketch(context, id + "F36", { "sketchPlane" : qUnion([Q0])});
            skLineSegment(sketch, "E64", {"start": v(-5292.17, 431.23) * mm, "end": v(-5292.17, -76.77) * mm});
            skLineSegment(sketch, "E65", {"start": v(-4809.57, -559.37) * mm, "end": v(-4809.57, -559.37) * mm});
            skLineSegment(sketch, "E66", {"start": v(-4326.97, -76.77) * mm, "end": v(-4326.97, 431.23) * mm});
            skLineSegment(sketch, "E67", {"start": v(-4809.57, 913.83) * mm, "end": v(-4809.57, 913.83) * mm});
            skPoint(sketch, "E68.visualSharp", {"position": v(-5292.17, 913.83) * mm});
            skArc(sketch, "E68.filletArc", {"start": v(-4809.57, 913.83) * mm, "mid": v(-5150.82, 772.48) * mm, "end": v(-5292.17, 431.23) * mm});
            skPoint(sketch, "E69.visualSharp", {"position": v(-4326.97, 913.83) * mm});
            skArc(sketch, "E69.filletArc", {"start": v(-4326.97, 431.23) * mm, "mid": v(-4468.32, 772.48) * mm, "end": v(-4809.57, 913.83) * mm});
            skPoint(sketch, "E70.visualSharp", {"position": v(-4326.97, -559.37) * mm});
            skArc(sketch, "E70.filletArc", {"start": v(-4809.57, -559.37) * mm, "mid": v(-4468.32, -418.02) * mm, "end": v(-4326.97, -76.77) * mm});
            skPoint(sketch, "E71.visualSharp", {"position": v(-5292.17, -559.37) * mm});
            skArc(sketch, "E71.filletArc", {"start": v(-5292.17, -76.77) * mm, "mid": v(-5150.82, -418.02) * mm, "end": v(-4809.57, -559.37) * mm});
            skSolve(sketch);
        }
        {
            var Q0;
            Q0 = qSketchRegion(id + "F36", true);
            extrude(context, id + "F37", {"entities" : qUnion([Q0]), "depth" : 25.4 * mm, "offsetDistance" : 25.4 * mm});
        }
        {
            var Q0;
            Q0=makeQuery(id+"F37.opExtrude","CAP_FACE",FACE,{"disambiguationData":[OSD([sQuery(id+"F36.wireOp",EDGE,"E64"),sQuery(id+"F36.wireOp",EDGE,"E66"),sQuery(id+"F36.wireOp",EDGE,"E68.filletArc"),sQuery(id+"F36.wireOp",EDGE,"E69.filletArc"),sQuery(id+"F36.wireOp",EDGE,"E70.filletArc"),sQuery(id+"F36.wireOp",EDGE,"E71.filletArc")])],"isStart":false});
            var sketch = newSketch(context, id + "F38", { "sketchPlane" : qUnion([Q0])});
            skArc(sketch, "E72.0", {"start": v(-4326.97, 431.23) * mm, "mid": v(-4809.57, 913.83) * mm, "end": v(-5292.17, 431.23) * mm});
            skLineSegment(sketch, "E73.0", {"start": v(-5292.17, 431.23) * mm, "end": v(-5292.17, -76.77) * mm});
            skArc(sketch, "E74.0", {"start": v(-5292.17, -76.77) * mm, "mid": v(-4809.57, -559.37) * mm, "end": v(-4326.97, -76.77) * mm});
            skLineSegment(sketch, "E75.0", {"start": v(-4326.97, -76.77) * mm, "end": v(-4326.97, 431.23) * mm});
            skArc(sketch, "E76.0", {"start": v(-4352.37, 431.23) * mm, "mid": v(-4809.57, 888.43) * mm, "end": v(-5266.77, 431.23) * mm});
            skLineSegment(sketch, "E76.1", {"start": v(-4352.37, -76.77) * mm, "end": v(-4352.37, 431.23) * mm});
            skArc(sketch, "E76.2", {"start": v(-5266.77, -76.77) * mm, "mid": v(-4809.57, -533.97) * mm, "end": v(-4352.37, -76.77) * mm});
            skLineSegment(sketch, "E76.3", {"start": v(-5266.77, 431.23) * mm, "end": v(-5266.77, -76.77) * mm});
            skSolve(sketch);
        }
        {
            var Q0;
            Q0 = qSketchRegion(id + "F38", true);
            extrude(context, id + "F39", {"entities" : qUnion([Q0]), "operationType" : NewBodyOperationType.ADD, "depth" : 6.35 * mm, "offsetDistance" : 25.4 * mm});
        }
        {
            var Q0;
            {var subQ0=sQuery(id+"F2.wireOp",EDGE,"E3.0");var subQ1=sQuery(id+"F2.wireOp",EDGE,"E2.0");var subQ2=sQuery(id+"F2.wireOp",EDGE,"E4.0");var subQ3=sQuery(id+"F2.wireOp",EDGE,"E1.0");var subQ4=sQuery(id+"F2.wireOp",EDGE,"E5.bottom");var subQ5=sQuery(id+"F2.wireOp",EDGE,"E5.top");var subQ6=sQuery(id+"F2.wireOp",EDGE,"E5.left");var subQ7=sQuery(id+"F2.wireOp",EDGE,"E5.right");Q0=makeQuery(id+"F27.boolean.opBoolean","SPLIT",FACE,{"disambiguationData":[TD([makeQuery(id+"F3.opExtrude","SWEPT_FACE",FACE,{"disambiguationData":[OSD([subQ3])]})])],"derivedFrom":makeQuery(id+"F3.opExtrude","CAP_FACE",FACE,{"disambiguationData":[OSD([subQ3,subQ1,subQ0,subQ2,subQ4,subQ5,subQ6,subQ7])],"isStart":false})});}
            var sketch = newSketch(context, id + "F40", { "sketchPlane" : qUnion([Q0])});
            skLineSegment(sketch, "E77.bottom", {"start": v(-1581.15, 1219.2) * mm, "end": v(-361.95, 1219.2) * mm});
            skLineSegment(sketch, "E77.top", {"start": v(-1581.15, 1117.6) * mm, "end": v(-361.95, 1117.6) * mm});
            skLineSegment(sketch, "E77.left", {"start": v(-1581.15, 1219.2) * mm, "end": v(-1581.15, 1117.6) * mm});
            skLineSegment(sketch, "E77.right", {"start": v(-361.95, 1219.2) * mm, "end": v(-361.95, 1117.6) * mm});
            skLineSegment(sketch, "E78", {"start": v(-971.55, 1219.2) * mm, "end": v(-971.55, 1117.6) * mm, "construction": true});
            skLineSegment(sketch, "E79.bottom", {"start": v(1016, 1219.2) * mm, "end": v(1930.4, 1219.2) * mm});
            skLineSegment(sketch, "E79.top", {"start": v(1016, 1117.6) * mm, "end": v(1930.4, 1117.6) * mm});
            skLineSegment(sketch, "E79.left", {"start": v(1016, 1219.2) * mm, "end": v(1016, 1117.6) * mm});
            skLineSegment(sketch, "E79.right", {"start": v(1930.4, 1219.2) * mm, "end": v(1930.4, 1117.6) * mm});
            skSolve(sketch);
        }
        {
            var Q0;
            Q0 = qSketchRegion(id + "F40", true);
            extrude(context, id + "F41", {"entities" : qUnion([Q0]), "operationType" : NewBodyOperationType.REMOVE, "oppositeDirection" : true, "depth" : 3.17 * mm, "offsetDistance" : 25.4 * mm});
        }
        {
            var Q0;
            Q0=makeQuery(id+"F1.opExtrude","CAP_FACE",FACE,{"disambiguationData":[OSD([sQuery(id+"F0.wireOp",EDGE,"E0.bottom"),sQuery(id+"F0.wireOp",EDGE,"E0.top"),sQuery(id+"F0.wireOp",EDGE,"E0.left"),sQuery(id+"F0.wireOp",EDGE,"E0.right")])],"isStart":false});
            var sketch = newSketch(context, id + "F42", { "sketchPlane" : qUnion([Q0])});
            skLineSegment(sketch, "E80.bottom", {"start": v(811.41, -355.6) * mm, "end": v(1319.41, -355.6) * mm});
            skLineSegment(sketch, "E80.top", {"start": v(811.41, -609.6) * mm, "end": v(1319.41, -609.6) * mm});
            skLineSegment(sketch, "E80.left", {"start": v(811.41, -355.6) * mm, "end": v(811.41, -609.6) * mm});
            skLineSegment(sketch, "E80.right", {"start": v(1319.41, -355.6) * mm, "end": v(1319.41, -609.6) * mm});
            skSolve(sketch);
        }
        {
            var Q0;
            Q0 = qSketchRegion(id + "F42", true);
            extrude(context, id + "F43", {"entities" : qUnion([Q0]), "depth" : 12.7 * mm, "offsetDistance" : 25.4 * mm});
        }
        {
            var Q0;
            Q0=makeQuery(id+"F1.opExtrude","CAP_FACE",FACE,{"disambiguationData":[OSD([sQuery(id+"F0.wireOp",EDGE,"E0.bottom"),sQuery(id+"F0.wireOp",EDGE,"E0.top"),sQuery(id+"F0.wireOp",EDGE,"E0.left"),sQuery(id+"F0.wireOp",EDGE,"E0.right")])],"isStart":false});
            var sketch = newSketch(context, id + "F44", { "sketchPlane" : qUnion([Q0])});
            skLineSegment(sketch, "E81", {"start": v(508, 382.8) * mm, "end": v(508, 319.3) * mm});
            skLineSegment(sketch, "E82", {"start": v(508, 319.3) * mm, "end": v(1266.3, 319.3) * mm});
            skLineSegment(sketch, "E83", {"start": v(1266.3, 319.3) * mm, "end": v(1266.3, 1117.6) * mm});
            skLineSegment(sketch, "E84", {"start": v(1266.3, 1117.6) * mm, "end": v(1202.8, 1117.6) * mm});
            skLineSegment(sketch, "E85", {"start": v(1202.8, 1117.6) * mm, "end": v(1202.8, 382.8) * mm});
            skLineSegment(sketch, "E86", {"start": v(1202.8, 382.8) * mm, "end": v(508, 382.8) * mm});
            skSolve(sketch);
        }
        {
            var Q0;
            Q0 = qSketchRegion(id + "F44", true);
            extrude(context, id + "F45", {"entities" : qUnion([Q0]), "depth" : 12.7 * mm, "offsetDistance" : 25.4 * mm});
        }
    });
